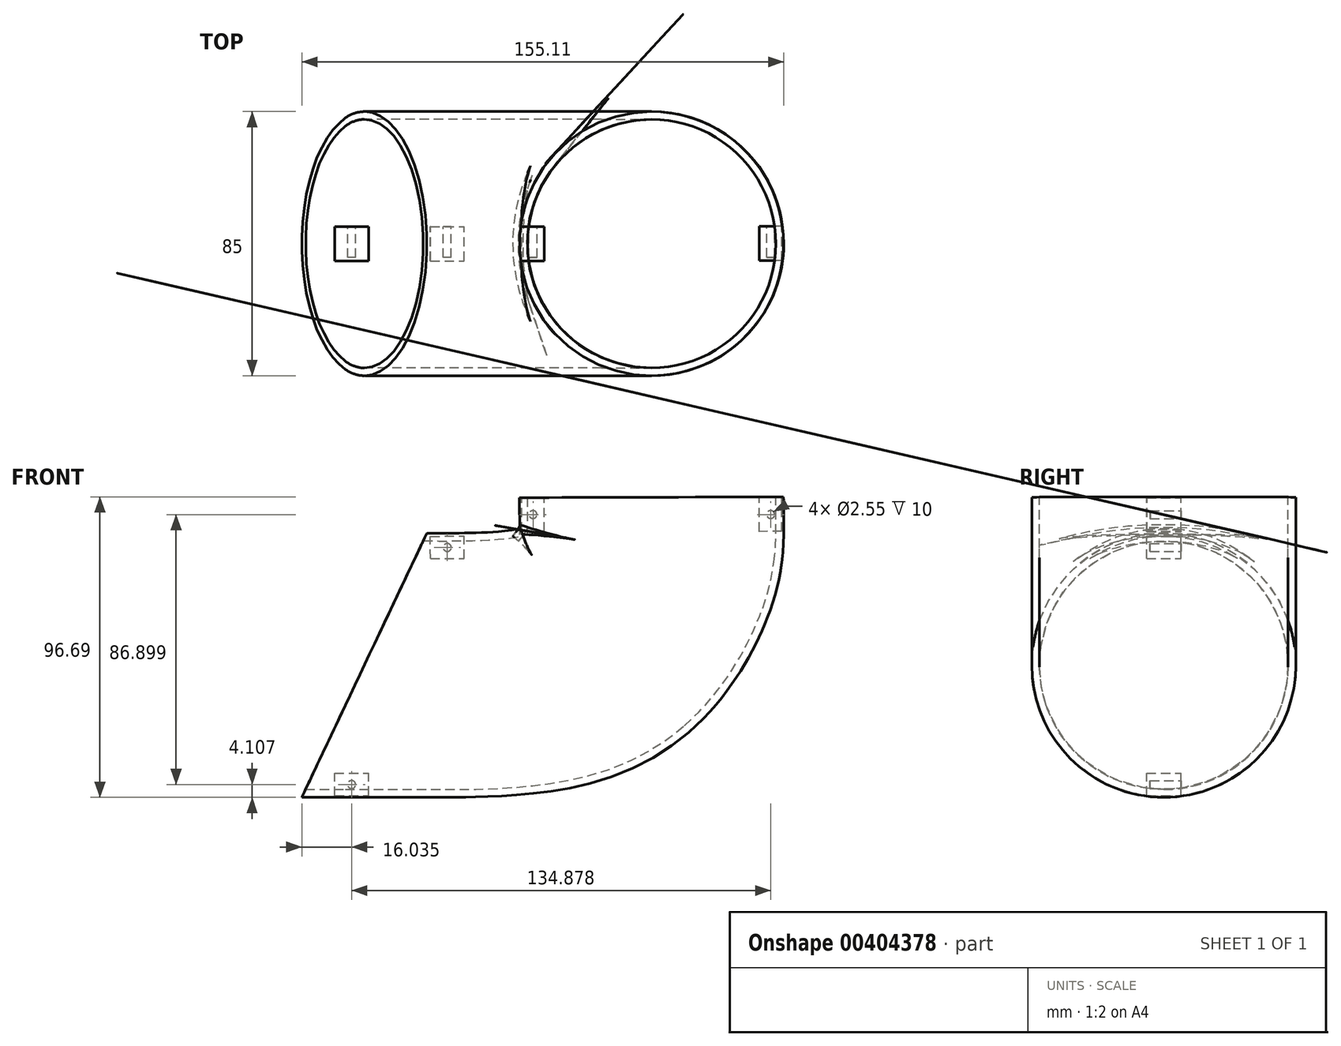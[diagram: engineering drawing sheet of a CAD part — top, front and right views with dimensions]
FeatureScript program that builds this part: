
annotation { "Feature Type Name" : "Feature", "Feature Type Description" : "" }
export const myFeature = defineFeature(function(context is Context, id is Id, definition is map)
    precondition{}
    {
        {
            var Q0;
            Q0=qCreatedBy(makeId("Front.planeOp"),FACE);
            var sketch = newSketch(context, id + "F0", { "sketchPlane" : qUnion([Q0])});
            skFitSpline(sketch, "E0", {"points": [v(-71.62, 0) * mm, v(-34.48, 0) * mm, v(-1.94, 3.84) * mm, v(16.96, 18.2) * mm, v(24.94, 34.6) * mm, v(25.95, 55) * mm], "startDerivative": vector(397.16, 0) * mm, "endDerivative": vector(-0.58, 200.1) * mm});
            skSolve(sketch);
        }
        {
            var Q0;
            Q0=qCreatedBy(makeId("Right.planeOp"),FACE);
            cPlane(context, id + "F1", {"entities" : qUnion([Q0]), "cplaneType" : CPlaneType.OFFSET, "offset" : 72.6 * mm, "oppositeDirection" : true, "width" : 150 * mm, "height" : 150 * mm});
        }
        {
            var Q0;
            Q0=qCreatedBy(id+"F1.planeOp",FACE);
            var sketch = newSketch(context, id + "F2", { "sketchPlane" : qUnion([Q0])});
            skCircle(sketch, "E1", {"center": v(0, 0) * mm, "radius": 42.5 * mm});
            skCircle(sketch, "E2", {"center": v(0, 0) * mm, "radius": 40 * mm});
            skSolve(sketch);
        }
        {
            var Q0;
            Q0=makeQuery(id+"F2.imprint","IMPRINT",FACE,{"disambiguationData":[TD([[makeQuery(id+"F2.imprint","IMPRINT",EDGE,{"derivedFrom":sQuery(id+"F2.wireOp",EDGE,"E1")}),1.0]])]});
            var Q1;
            Q1=sQuery(id+"F0.wireOp",EDGE,"E0");
            sweep(context, id + "F3", {"profiles" : qUnion([Q0]), "path" : qUnion([Q1])});
        }
        {
            var Q0;
            Q0=makeQuery(id+"F3.opSweep","CAP_FACE",FACE,{"disambiguationData":[OSD([sQuery(id+"F0.wireOp",VERTEX,"E0.end"),sQuery(id+"F2.wireOp",EDGE,"E1"),sQuery(id+"F2.wireOp",EDGE,"E2")])],"isStart":false});
            cPlane(context, id + "F4", {"entities" : qUnion([Q0]), "cplaneType" : CPlaneType.OFFSET, "offset" : 0 * mm, "width" : 150 * mm, "height" : 150 * mm});
        }
        {
            var Q0;
            Q0=qCreatedBy(id+"F4.planeOp",FACE);
            var sketch = newSketch(context, id + "F5", { "sketchPlane" : qUnion([Q0])});
            skLineSegment(sketch, "E3.bottom", {"start": v(-8.65, -5.52) * mm, "end": v(-15.87, -5.52) * mm});
            skLineSegment(sketch, "E3.top", {"start": v(-8.65, 5.52) * mm, "end": v(-15.87, 5.52) * mm});
            skLineSegment(sketch, "E3.left", {"start": v(-8.65, -5.52) * mm, "end": v(-8.65, 5.52) * mm});
            skLineSegment(sketch, "E3.right", {"start": v(-15.87, -5.52) * mm, "end": v(-15.87, 5.52) * mm});
            skPoint(sketch, "E3.middle", {"position": v(-12.26, 0) * mm});
            skSolve(sketch);
        }
        {
            var Q0;
            Q0=makeQuery(id+"F5.imprint","IMPRINT",FACE,{"disambiguationData":[TD([[makeQuery(id+"F5.imprint","IMPRINT",EDGE,{"derivedFrom":sQuery(id+"F5.wireOp",EDGE,"E3.bottom")}),-1.0]])]});
            extrude(context, id + "F6", {"entities" : qUnion([Q0]), "oppositeDirection" : true, "depth" : 10.9 * mm});
        }
        {
            var Q0;
            Q0=makeQuery(id+"F6.opExtrude","SWEPT_BODY",BODY,{"disambiguationData":[OSD([sQuery(id+"F5.wireOp",EDGE,"E3.bottom"),sQuery(id+"F5.wireOp",EDGE,"E3.top"),sQuery(id+"F5.wireOp",EDGE,"E3.left"),sQuery(id+"F5.wireOp",EDGE,"E3.right")])]});
            transform(context, id + "F7", {"entities" : qUnion([Q0]), "transformType" : TransformType.TRANSLATION_3D, "dx" : 80.4 * mm, "dy" : 39.2 * mm, "dz" : 0 * mm, "makeCopy" : false});
        }
        {
            var Q0;
            Q0=makeQuery(id+"F6.opExtrude","SWEPT_FACE",FACE,{"disambiguationData":[OSD([sQuery(id+"F5.wireOp",EDGE,"E3.top")])]});
            var sketch = newSketch(context, id + "F8", { "sketchPlane" : qUnion([Q0])});
            skLineSegment(sketch, "E4", {"start": v(-68.01, 43) * mm, "end": v(-68.01, 17.67) * mm, "construction": true});
            skLineSegment(sketch, "E5", {"start": v(-71.6, 48.47) * mm, "end": v(-50.76, 48.4) * mm, "construction": true});
            skCircle(sketch, "E6", {"center": v(-68.01, 48.46) * mm, "radius": 1.28 * mm});
            skSolve(sketch);
        }
        {
            var Q0;
            Q0=makeQuery(id+"F8.imprint","IMPRINT",FACE,{"disambiguationData":[TD([[makeQuery(id+"F8.imprint","IMPRINT",EDGE,{"derivedFrom":sQuery(id+"F8.wireOp",EDGE,"E6")}),1.0]])]});
            extrude(context, id + "F9", {"entities" : qUnion([Q0]), "operationType" : NewBodyOperationType.REMOVE, "oppositeDirection" : true, "depth" : 10 * mm});
        }
        {
            var Q0;
            Q0=makeQuery(id+"F6.opExtrude","SWEPT_BODY",BODY,{"disambiguationData":[OSD([sQuery(id+"F5.wireOp",EDGE,"E3.bottom"),sQuery(id+"F5.wireOp",EDGE,"E3.top"),sQuery(id+"F5.wireOp",EDGE,"E3.left"),sQuery(id+"F5.wireOp",EDGE,"E3.right")])]});
            transform(context, id + "F10", {"entities" : qUnion([Q0]), "transformType" : TransformType.TRANSLATION_3D, "dx" : -3.7 * mm, "dy" : -39.1 * mm, "dz" : 0 * mm, "makeCopy" : true});
        }
        {
            var Q0;
            Q0=makeQuery(id+"F6.opExtrude","SWEPT_BODY",BODY,{"disambiguationData":[OSD([sQuery(id+"F5.wireOp",EDGE,"E3.bottom"),sQuery(id+"F5.wireOp",EDGE,"E3.top"),sQuery(id+"F5.wireOp",EDGE,"E3.left"),sQuery(id+"F5.wireOp",EDGE,"E3.right")])]});
            transform(context, id + "F11", {"entities" : qUnion([Q0]), "transformType" : TransformType.TRANSLATION_3D, "dx" : -80.2 * mm, "dy" : -39.2 * mm, "dz" : 0 * mm, "makeCopy" : false});
        }
        {
            var Q0;
            Q0=qCreatedBy(makeId("Front.planeOp"),FACE);
            var sketch = newSketch(context, id + "F12", { "sketchPlane" : qUnion([Q0])});
            skLineSegment(sketch, "E7", {"start": v(-45.65, 43.93) * mm, "end": v(-89.43, 43.93) * mm});
            skLineSegment(sketch, "E8", {"start": v(-89.43, 43.93) * mm, "end": v(-89.43, -48.48) * mm});
            skLineSegment(sketch, "E9", {"start": v(-89.43, -48.48) * mm, "end": v(-45.65, 43.93) * mm});
            skSolve(sketch);
        }
        {
            var Q0;
            {var subQ0=sQuery(id+"F2.wireOp",EDGE,"E2");var subQ1=sQuery(id+"F2.wireOp",EDGE,"E1");Q0=makeQuery(id+"FLzqFWgApmgUHHJ_0.boolean.opBoolean","MERGE",FACE,{"derivedFrom":[makeQuery(id+"F3.opSweep","CAP_FACE",FACE,{"disambiguationData":[OSD([sQuery(id+"F0.wireOp",VERTEX,"E0.start"),subQ1,subQ0])],"isStart":true}),makeQuery(id+"FLzqFWgApmgUHHJ_0.opExtrude","CAP_FACE",FACE,{"disambiguationData":[OSD([subQ1,subQ0])],"isStart":true})]});}
            extrude(context, id + "F13", {"entities" : qUnion([Q0]), "operationType" : NewBodyOperationType.ADD, "depth" : 15 * mm});
        }
        {
            var Q0;
            Q0=makeQuery(id+"F12.imprint","IMPRINT",FACE,{"disambiguationData":[TD([[makeQuery(id+"F12.imprint","IMPRINT",EDGE,{"derivedFrom":sQuery(id+"F12.wireOp",EDGE,"E7")}),1.0]])]});
            extrude(context, id + "F14", {"entities" : qUnion([Q0]), "operationType" : NewBodyOperationType.REMOVE, "endBound" : BoundingType.SYMMETRIC, "depth" : 99.8 * mm});
        }
        {
            var Q0;
            Q0=makeQuery(id+"F6.opExtrude","SWEPT_BODY",BODY,{"disambiguationData":[OSD([sQuery(id+"F5.wireOp",EDGE,"E3.bottom"),sQuery(id+"F5.wireOp",EDGE,"E3.top"),sQuery(id+"F5.wireOp",EDGE,"E3.left"),sQuery(id+"F5.wireOp",EDGE,"E3.right")])]});
            transform(context, id + "F15", {"entities" : qUnion([Q0]), "transformType" : TransformType.TRANSLATION_3D, "dx" : -62.2 * mm, "dy" : 0 * mm, "dz" : -84.3 * mm, "makeCopy" : true});
        }
        {
            var Q0;
            Q0=makeQuery(id+"F15.opPattern","COPY",BODY,{"derivedFrom":makeQuery(id+"F6.opExtrude","SWEPT_BODY",BODY,{"disambiguationData":[OSD([sQuery(id+"F5.wireOp",EDGE,"E3.bottom"),sQuery(id+"F5.wireOp",EDGE,"E3.top"),sQuery(id+"F5.wireOp",EDGE,"E3.left"),sQuery(id+"F5.wireOp",EDGE,"E3.right")])]}),"instanceName":"1"});
            var Q1;
            Q1=makeQuery(id+"F15.opPattern","COPY",EDGE,{"derivedFrom":makeQuery(id+"F6.opExtrude","CAP_EDGE",EDGE,{"disambiguationData":[OSD([sQuery(id+"F5.wireOp",EDGE,"E3.right")])],"isStart":true}),"instanceName":"1"});
            transform(context, id + "F16", {"entities" : qUnion([Q0]), "transformType" : TransformType.ROTATION, "transformAxis" : qUnion([Q1]), "angle" : 90 * degree, "makeCopy" : false});
        }
        {
            var Q0;
            Q0=makeQuery(id+"F15.opPattern","COPY",BODY,{"derivedFrom":makeQuery(id+"F6.opExtrude","SWEPT_BODY",BODY,{"disambiguationData":[OSD([sQuery(id+"F5.wireOp",EDGE,"E3.bottom"),sQuery(id+"F5.wireOp",EDGE,"E3.top"),sQuery(id+"F5.wireOp",EDGE,"E3.left"),sQuery(id+"F5.wireOp",EDGE,"E3.right")])]}),"instanceName":"1"});
            transform(context, id + "F17", {"entities" : qUnion([Q0]), "transformType" : TransformType.TRANSLATION_3D, "dx" : 12.9 * mm, "dy" : 0 * mm, "dz" : -4.4 * mm, "makeCopy" : false});
        }
        {
            var Q0;
            Q0=makeQuery(id+"F15.opPattern","COPY",BODY,{"derivedFrom":makeQuery(id+"F6.opExtrude","SWEPT_BODY",BODY,{"disambiguationData":[OSD([sQuery(id+"F5.wireOp",EDGE,"E3.bottom"),sQuery(id+"F5.wireOp",EDGE,"E3.top"),sQuery(id+"F5.wireOp",EDGE,"E3.left"),sQuery(id+"F5.wireOp",EDGE,"E3.right")])]}),"instanceName":"1"});
            transform(context, id + "F18", {"entities" : qUnion([Q0]), "transformType" : TransformType.TRANSLATION_3D, "dx" : 30.8 * mm, "dy" : 0 * mm, "dz" : 76.3 * mm, "makeCopy" : true});
        }
    });
